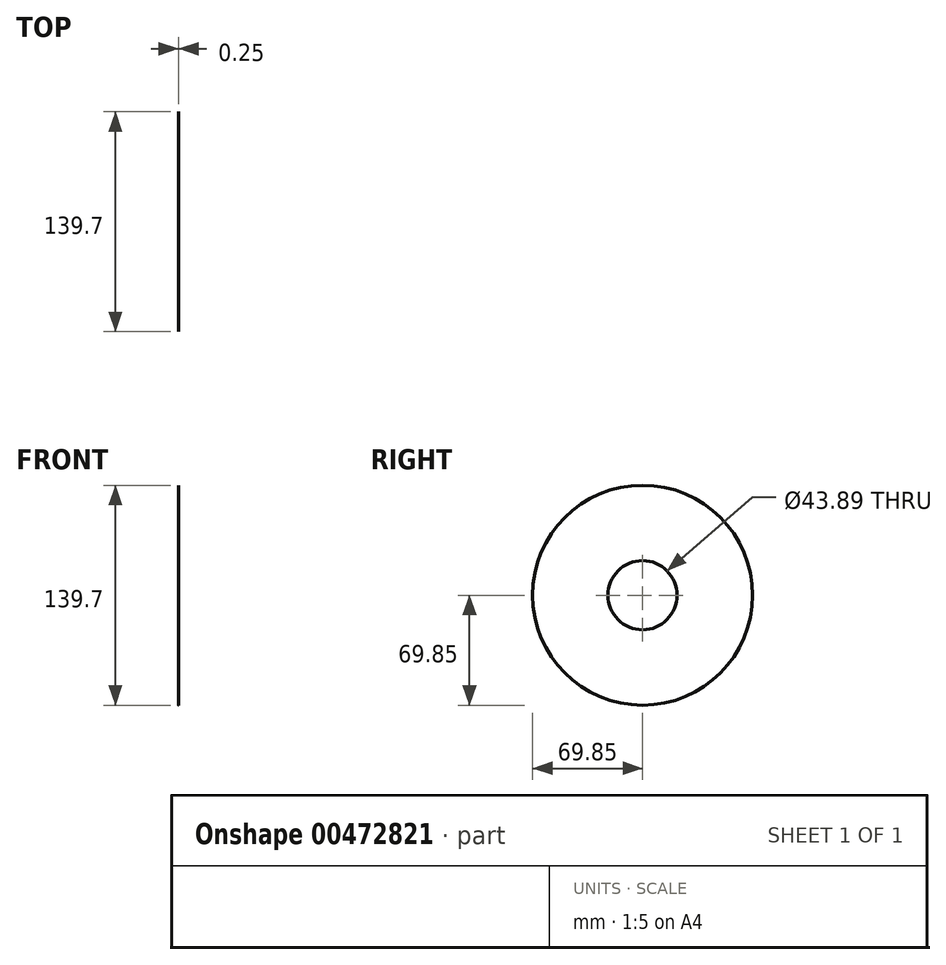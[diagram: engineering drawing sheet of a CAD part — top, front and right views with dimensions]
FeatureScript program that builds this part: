
annotation { "Feature Type Name" : "Feature", "Feature Type Description" : "" }
export const myFeature = defineFeature(function(context is Context, id is Id, definition is map)
    precondition{}
    {
        {
            assignVariable(context, id + "F0", {"name" : "Thick", "anyValue" : .25});
        }
        {
            var Q0;
            Q0=qCreatedBy(makeId("Right.planeOp"),FACE);
            var sketch = newSketch(context, id + "F1", { "sketchPlane" : qUnion([Q0])});
            skCircle(sketch, "E0", {"center": v(0, 0) * mm, "radius": 69.85 * mm});
            skCircle(sketch, "E1", {"center": v(0, 0) * mm, "radius": 21.94 * mm});
            skSolve(sketch);
        }
        {
            var Q0;
            Q0=makeQuery(id+"F1.imprint","IMPRINT",FACE,{"disambiguationData":[TD([[makeQuery(id+"F1.imprint","IMPRINT",EDGE,{"derivedFrom":sQuery(id+"F1.wireOp",EDGE,"E0")}),1.0]])]});
            extrude(context, id + "F2", {"entities" : qUnion([Q0]), "depth" : (getVariable(context, 'Thick')) * mm});
        }
    });
